SOLIDWORKS PART (.sldprt)
format: sldprt  version: not decoded by parser v0  size: 227,840 bytes
history: native  units: mm
features: sketch x8, extrude x4, plane x3, sweep x2, material x1, helix x1 (+10 scaffold rows collapsed)
feature tree (29):
  scaffold x10  (default folders/planes/origin — collapsed)
  material  "Matériau <non spécifié>"
  plane  "Plan1"
  plane  "Plan2"
  plane  "Plan3"
  sketch  "Esquisse1"  dims[Dt=26.946mm]
  extrude  "Base-Extrusion"  Depth=62mm
  sketch  "EsquisseR"  dims[D1=16.5mm]
  extrude  "RaccordD"  Depth=1.5mm
  sketch  "Esquisse8"  dims[D1=0.0mm]
  extrude  "RaccordG"  Depth=1.5mm
  sketch  "Construction"  dims[c1.Dp=3.75mm c1.D1=22.0mm c2.D1=~14.036243deg c2.ap=349.0mm c2.Dn=11.473mm c3.D1=3.1535mm c3.D2=~14.01192mm c3.Dp=8.973mm c3.px=6.307mm]
  sketch  "Esquisse3"  dims[Dn=22.946mm]
  helix  "Hélice1G"  Pitch=34.1535mm
  sketch  "Esquisse5"  dims[D1=0.0mm]
  extrude  "Hélice1D"  Depth=34.1535mm
  sketch  "Filet1G"
  sketch  "Filet1D"  dims[D1=0.0mm]
  sweep  "Enlèvement de matière-Balayage1"
  sweep  "Enlèvement de matière-Balayage2"
decode coverage: 12 of 15 modeling features carry decoded parameters
note: ~ marks probable driven/reference dimensions
note: suppression state not decoded; provenance and decode notes live in map.json
